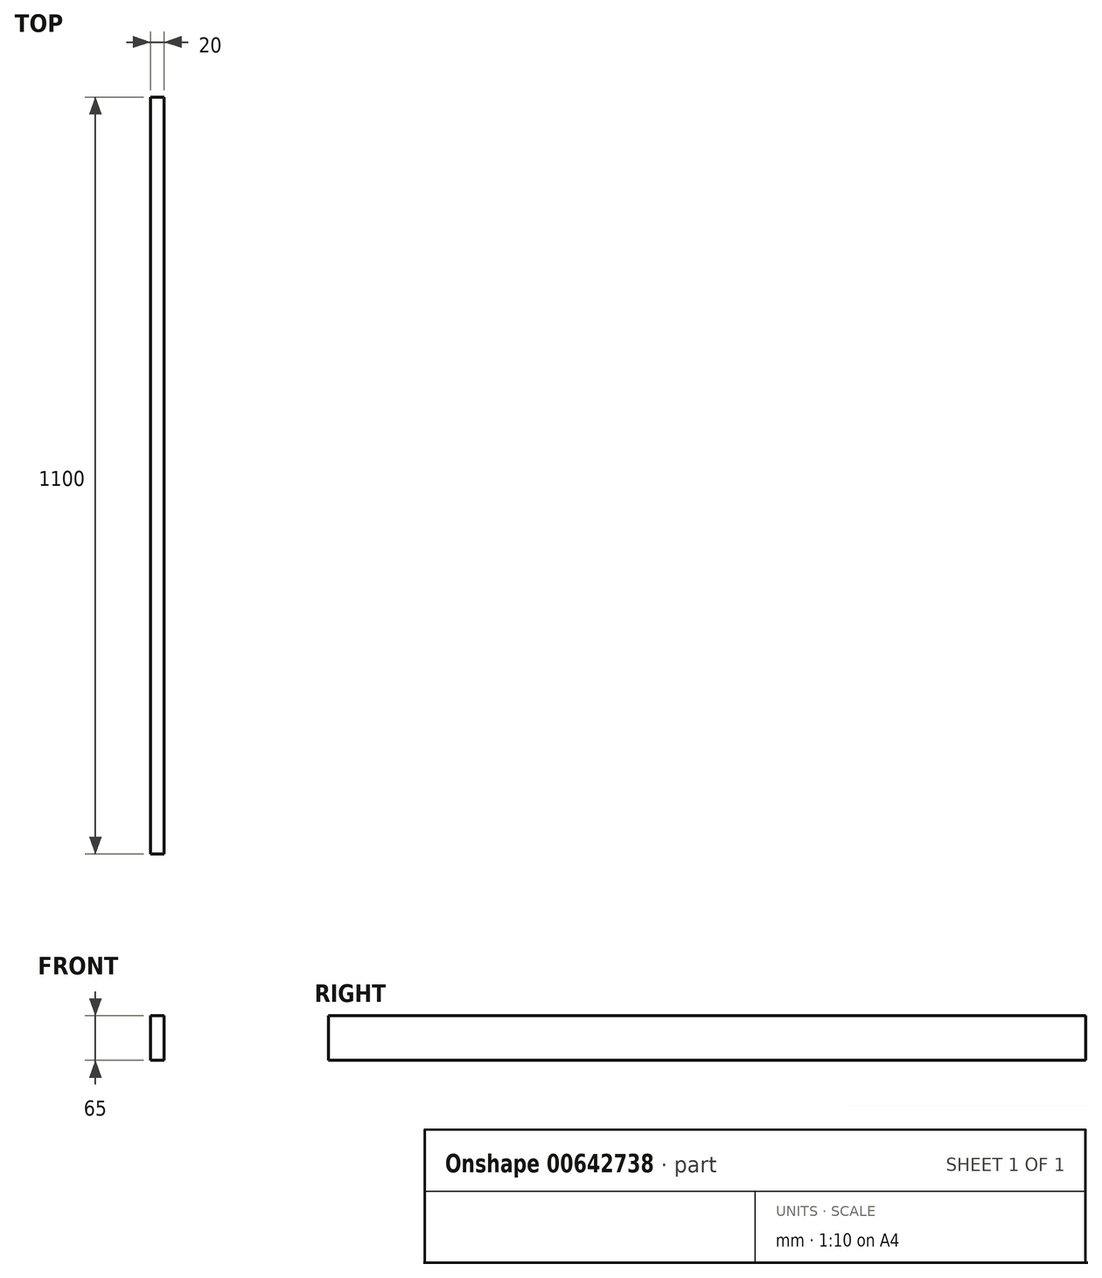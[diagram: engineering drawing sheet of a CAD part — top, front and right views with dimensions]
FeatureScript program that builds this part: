
annotation { "Feature Type Name" : "Feature", "Feature Type Description" : "" }
export const myFeature = defineFeature(function(context is Context, id is Id, definition is map)
    precondition{}
    {
        {
            var Q0;
            Q0=qCreatedBy(makeId("Front.planeOp"),FACE);
            var sketch = newSketch(context, id + "F0", { "sketchPlane" : qUnion([Q0])});
            skLineSegment(sketch, "E0.bottom", {"start": v(0, 0) * mm, "end": v(20, 0) * mm});
            skLineSegment(sketch, "E0.top", {"start": v(0, 65) * mm, "end": v(20, 65) * mm});
            skLineSegment(sketch, "E0.left", {"start": v(0, 0) * mm, "end": v(0, 65) * mm});
            skLineSegment(sketch, "E0.right", {"start": v(20, 0) * mm, "end": v(20, 65) * mm});
            skSolve(sketch);
        }
        {
            var Q0;
            Q0 = qSketchRegion(id + "F0", true);
            extrude(context, id + "F1", {"entities" : qUnion([Q0]), "depth" : 1100 * mm, "offsetDistance" : 25 * mm});
        }
    });
